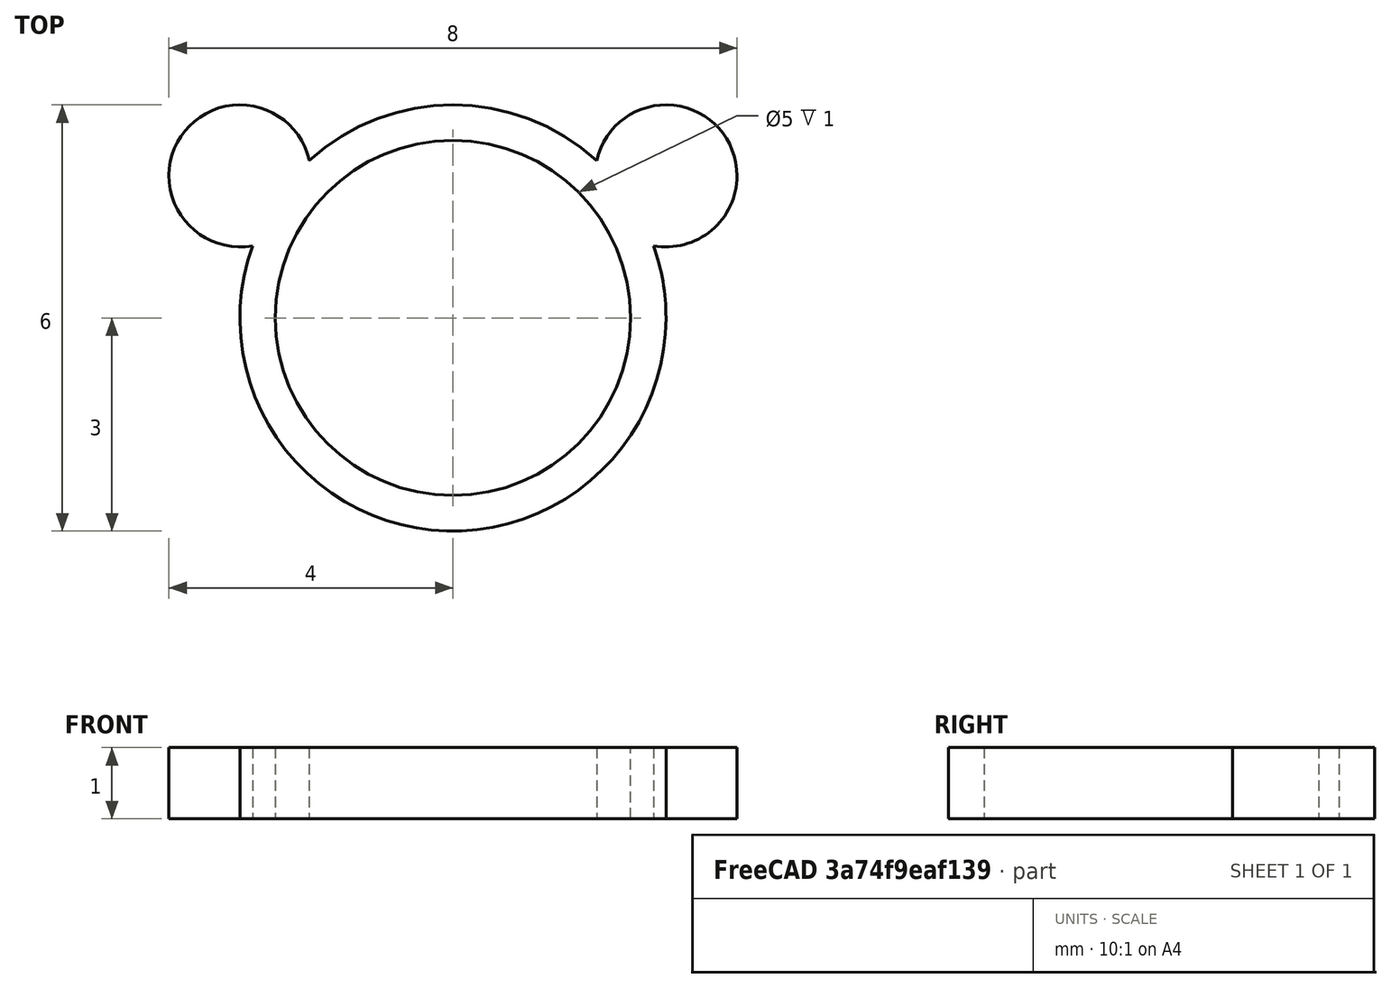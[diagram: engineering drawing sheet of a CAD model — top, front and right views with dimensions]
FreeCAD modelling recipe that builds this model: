
FCSTD DOCUMENT  (FreeCAD 0.19R)
Label: Reto 6
License: All rights reserved
LicenseURL: http://en.wikipedia.org/wiki/All_rights_reserved
objects: App::MeasureDistance×9, Part::Cylinder×4, Part::Cut×1, Part::MultiFuse×1
note: 6 computed .brp shape members not serialized (recipe doc carries the construction recipe); baked Part::Feature solids carry a one-line shape summary decoded from their .brp

FEATURE [Part::Cylinder] Cylinder  label="Cilindro"
  Angle = 360
  AttacherType = Attacher::AttachEngine3D
  Height = 1
  Radius = 3
FEATURE [Part::Cylinder] Cylinder001  label="Cilindro001"
  Angle = 360
  AttacherType = Attacher::AttachEngine3D
  Height = 1
  Placement = pos=(0,0,-3) rot=(0,0,1;0rad)
  Radius = 3
FEATURE [Part::Cut] Cut
  Base = -> Cylinder
  Refine = true
  Tool = -> Cylinder001
FEATURE [Part::Cylinder] Cylinder002  label="Cilindro002"
  Angle = 360
  AttacherType = Attacher::AttachEngine3D
  Height = 1
  Placement = pos=(-3,2,0) rot=(0,0,1;0rad)
  Radius = 1
FEATURE [Part::Cylinder] Cylinder003  label="Cilindro003"
  Angle = 360
  AttacherType = Attacher::AttachEngine3D
  Height = 1
  Placement = pos=(3,2,0) rot=(0,0,1;0rad)
  Radius = 1
FEATURE [App::MeasureDistance] Distance  label="Distance: 1,44 mm"
  Distance = 1.44115
  P1 = (-2.02337,2.21494,1)
  P2 = (-2.82278,1.01583,1)
FEATURE [App::MeasureDistance] Distance001  label="Distance: 4,98 mm"
  Distance = 4.98468
  P1 = (-0.0628656,2.49381,1)
  P2 = (0.131005,-2.4871,1)
FEATURE [App::MeasureDistance] Distance002  label="Distance: 1,99 mm"
  Distance = 1.99061
  P1 = (-2.35181,2.75204,1)
  P2 = (-3.7214,1.30748,1)
FEATURE [App::MeasureDistance] Distance003  label="Distance: 5,98 mm"
  Distance = 5.97994
  P1 = (0.0223212,2.98986,1)
  P2 = (0.126483,-2.98917,1)
FEATURE [App::MeasureDistance] Distance004  label="Distance: 2,10 mm"
  Distance = 2.10284
  P1 = (3.77574,2.62282,1)
  P2 = (2.03873,1.4376,1)
FEATURE [App::MeasureDistance] Distance005  label="Distance: 1,00 mm"
  Distance = 1.00275
  P1 = (-3.42276,1.1021,1)
  P2 = (-3.35548,1.07068,0)
FEATURE [App::MeasureDistance] Distance006  label="Distance: 1,00 mm001"
  Distance = 1.00146
  P1 = (0.33184,-2.97088,1)
  P2 = (0.385669,-2.96609,0)
FEATURE [App::MeasureDistance] Distance007  label="Distance: 2,02 mm"
  Distance = 2.01727
  P1 = (-3.1439,2.987,0.511679)
  P2 = (-2.8282,0.995307,0.457849)
FEATURE [Part::MultiFuse] Fusion  label="Reto 6"
  Refine = true
  Shapes = -> [Cut,Cylinder002,Cylinder003]
FEATURE [App::MeasureDistance] Distance008  label="Distance: 3,14 mm"
  Distance = 3.13632
  P1 = (-3.10124,1.00876,0.282904)
  P2 = (-2.23491,-1.99223,0)
